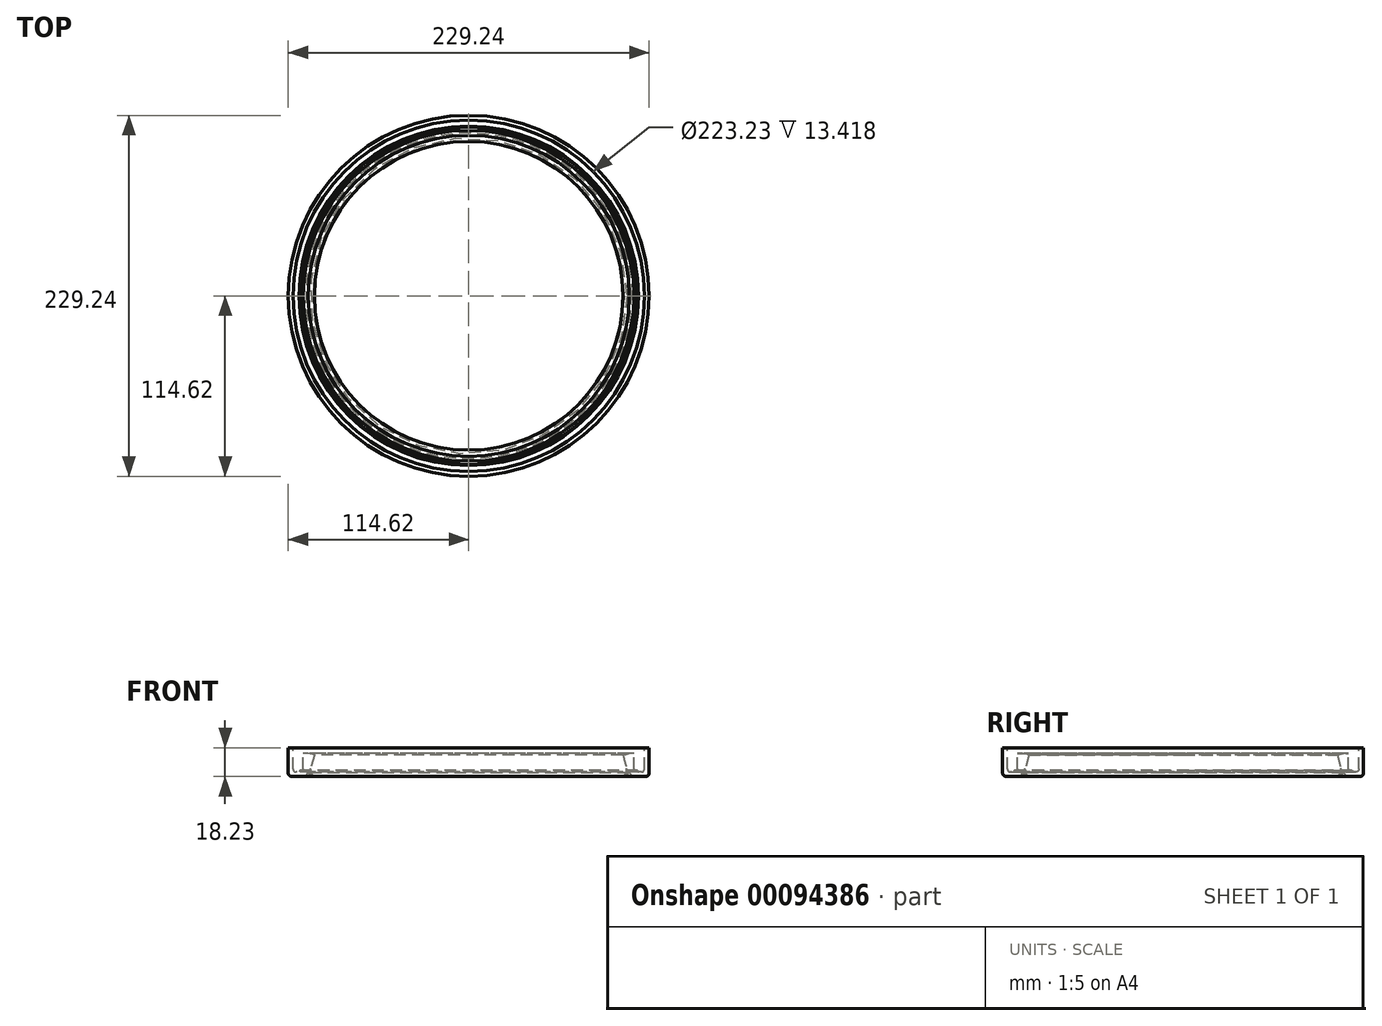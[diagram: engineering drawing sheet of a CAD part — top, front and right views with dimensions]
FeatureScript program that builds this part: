
annotation { "Feature Type Name" : "Feature", "Feature Type Description" : "" }
export const myFeature = defineFeature(function(context is Context, id is Id, definition is map)
    precondition{}
    {
        {
            var Q0;
            Q0=qCreatedBy(makeId("Front.planeOp"),FACE);
            var sketch = newSketch(context, id + "F0", { "sketchPlane" : qUnion([Q0])});
            skLineSegment(sketch, "E0", {"start": v(-112.62, 0) * mm, "end": v(-112.62, -10) * mm});
            skLineSegment(sketch, "E1", {"start": v(-109.62, -13) * mm, "end": v(-103.62, -13) * mm});
            skLineSegment(sketch, "E2", {"start": v(-103.62, -13) * mm, "end": v(-103.62, -12) * mm});
            skLineSegment(sketch, "E3", {"start": v(-103.62, -12) * mm, "end": v(-109.62, -12) * mm});
            skLineSegment(sketch, "E4", {"start": v(-111.62, -10) * mm, "end": v(-111.62, 0) * mm});
            skLineSegment(sketch, "E5", {"start": v(-111.62, 0) * mm, "end": v(-112.62, 0) * mm});
            skPoint(sketch, "E6.visualSharp", {"position": v(-111.62, -12) * mm});
            skArc(sketch, "E6.filletArc", {"start": v(-111.62, -10) * mm, "mid": v(-111.03, -11.41) * mm, "end": v(-109.62, -12) * mm});
            skPoint(sketch, "E7.visualSharp", {"position": v(-112.62, -13) * mm});
            skArc(sketch, "E7.filletArc", {"start": v(-112.62, -10) * mm, "mid": v(-111.74, -12.12) * mm, "end": v(-109.62, -13) * mm});
            skLineSegment(sketch, "E8", {"start": v(-111.62, 0) * mm, "end": v(-111.62, 3.42) * mm});
            skLineSegment(sketch, "E9", {"start": v(-111.62, 3.42) * mm, "end": v(-114.62, 3.42) * mm});
            skLineSegment(sketch, "E10", {"start": v(-114.62, 3.42) * mm, "end": v(-114.62, -12.66) * mm});
            skLineSegment(sketch, "E11", {"start": v(-112.62, -14.66) * mm, "end": v(-103.4, -14.66) * mm});
            skLineSegment(sketch, "E12", {"start": v(-103.4, -14.66) * mm, "end": v(-102.5, -12.81) * mm});
            skLineSegment(sketch, "E13", {"start": v(-101.52, -12.67) * mm, "end": v(-99.6, -14.77) * mm});
            skLineSegment(sketch, "E14", {"start": v(-99.46, -14.78) * mm, "end": v(-98.84, -14.2) * mm});
            skLineSegment(sketch, "E15", {"start": v(-98.83, -14.07) * mm, "end": v(-99.4, -13.45) * mm});
            skLineSegment(sketch, "E16", {"start": v(-100.3, -9.7) * mm, "end": v(-98, -1.15) * mm});
            skLineSegment(sketch, "E17", {"start": v(-98, -1.15) * mm, "end": v(-101.92, 0) * mm});
            skLineSegment(sketch, "E18", {"start": v(-101.92, 0) * mm, "end": v(-105.07, 0) * mm});
            skLineSegment(sketch, "E19", {"start": v(-105.07, 0) * mm, "end": v(-105.07, -10) * mm});
            skLineSegment(sketch, "E20", {"start": v(-105.52, -10.59) * mm, "end": v(-107.07, -10.99) * mm});
            skLineSegment(sketch, "E21", {"start": v(-107.07, -10.99) * mm, "end": v(-107.71, -12) * mm});
            skPoint(sketch, "E22.visualSharp", {"position": v(-100.88, -11.83) * mm});
            skArc(sketch, "E22.filletArc", {"start": v(-100.3, -9.7) * mm, "mid": v(-100.33, -11.7) * mm, "end": v(-99.4, -13.45) * mm});
            skPoint(sketch, "E23.visualSharp", {"position": v(-102.11, -12.02) * mm});
            skArc(sketch, "E23.filletArc", {"start": v(-101.52, -12.67) * mm, "mid": v(-102.05, -12.48) * mm, "end": v(-102.5, -12.81) * mm});
            skPoint(sketch, "E24.visualSharp", {"position": v(-105.07, -10.47) * mm});
            skArc(sketch, "E24.filletArc", {"start": v(-105.52, -10.59) * mm, "mid": v(-105.2, -10.37) * mm, "end": v(-105.07, -10) * mm});
            skPoint(sketch, "E25.visualSharp", {"position": v(-114.62, -14.66) * mm});
            skArc(sketch, "E25.filletArc", {"start": v(-114.62, -12.66) * mm, "mid": v(-114.03, -14.07) * mm, "end": v(-112.62, -14.66) * mm});
            skPoint(sketch, "E26.visualSharp", {"position": v(-98.77, -14.14) * mm});
            skArc(sketch, "E26.filletArc", {"start": v(-98.84, -14.2) * mm, "mid": v(-98.8, -14.14) * mm, "end": v(-98.83, -14.07) * mm});
            skPoint(sketch, "E27.visualSharp", {"position": v(-99.54, -14.85) * mm});
            skArc(sketch, "E27.filletArc", {"start": v(-99.6, -14.77) * mm, "mid": v(-99.54, -14.8) * mm, "end": v(-99.46, -14.78) * mm});
            skLineSegment(sketch, "E28", {"start": v(0, 34.78) * mm, "end": v(0, -47.98) * mm, "construction": true});
            skSolve(sketch);
        }
        {
            var Q0;
            Q0=makeQuery(id+"F0.imprint","IMPRINT",FACE,{"disambiguationData":[TD([[makeQuery(id+"F0.imprint","IMPRINT",EDGE,{"derivedFrom":sQuery(id+"F0.wireOp",EDGE,"E0")}),1.0]])]});
            var Q1;
            Q1=sQuery(id+"F0.wireOp",EDGE,"E28");
            revolve(context, id + "F1", {"entities" : qUnion([Q0]), "axis" : qUnion([Q1]), "revolveType" : RevolveType.FULL});
        }
        {
            var Q0;
            Q0=makeQuery(id+"F0.imprint","IMPRINT",FACE,{"disambiguationData":[TD([[makeQuery(id+"F0.imprint","IMPRINT",EDGE,{"derivedFrom":sQuery(id+"F0.wireOp",EDGE,"E0")}),-1.0]])]});
            var Q1;
            Q1=sQuery(id+"F0.wireOp",EDGE,"E28");
            revolve(context, id + "F2", {"operationType" : NewBodyOperationType.ADD, "entities" : qUnion([Q0]), "axis" : qUnion([Q1]), "revolveType" : RevolveType.FULL});
        }
    });
